# Revit family: P3843-77 3-75W CONVERTIBLE SEMI-FLSH
name_source: partatom
category: Lighting Fixtures
revit_build: Autodesk Revit Architecture 2012 (Build: 20110309_2315(x64)
units: mm (PartAtom-declared; Revit-internal decimal feet)

## types (1)
- P3843-77 3-75W CONVERTIBLE SEMI-FLSH
    Back Plate = Forged Bronze
    Ceiling Chain = Forged Bronze
    Celing chain length = 63.00"
    Default Elevation = 48.00"
    Description = Three-light semi-flush with etched white oversized, bell-shaped glass bowl. Distinctive ebbing and flowing of squared scrolls and arms in Brushed Nickel finish.
    Glass = Ethed Albastor Glass Shade
    Lamp = Three
    Manufacturer = Progress Lighting
    Manufacturer Fax = (864)-678-1065
    Model = P3843-77
    Mounting = Ceiling Semi-Flush Mount
    Product Documentation Link = https://progresslighting.com
    Product Page URL = https://progresslighting.com
    URL = http://www.progresslighting.com
    Wattage Comments = 75W

## geometry (parser evidence)
native form markers: Blend x1, Sweep x6
no freeform markers — native parametric forms only
